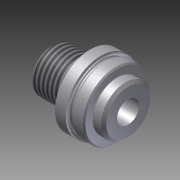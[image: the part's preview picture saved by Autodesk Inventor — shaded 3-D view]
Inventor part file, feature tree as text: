
AUTODESK INVENTOR PART (.ipt)
format: ipt  version: 2012 (Build 160160000, 160)  size: 204,288 bytes
history: native  units: in
note: dims shown in document units (in); Inventor stores cm internally (conversion verified against a paired STEP export)
features: other x70, sketch x5, revolve x4, thread x1, hole x1
ambient origin geometry x8: Origin, YZ Plane, XZ Plane, XY Plane, X Axis, Y Axis, Z Axis, Center Point
bodies: Solid1 (feature_tree)
feature tree (81):
  revolve  "Revolution1"  [1 undecoded]
  thread  "Thread1"  [1 undecoded]
  revolve  "Revolution2"  Angle=360.0deg
  revolve  "Revolution3"  [1 undecoded]
  hole  "Drilling 1"  [1 undecoded]
  revolve  "Revolution4"  [1 undecoded]
  other  "rod_guide_XY"
  other  "rod_guide_YZ"
  other  "rod_guide_ZX"
  other  "rod_guide_X"
  other  "rod_guide_Y"
  other  "rod_guide_Z"
  other  "rod_guide_Center"
  other  "to_tube_XY"
  other  "to_tube_YZ"
  other  "to_tube_ZX"
  other  "to_tube_X"
  other  "to_tube_Y"
  other  "to_tube_Z"
  other  "to_tube_Center"
  other  "to_foot_bracket_XY"
  other  "to_foot_bracket_YZ"
  other  "to_foot_bracket_ZX"
  other  "to_foot_bracket_X"
  other  "to_foot_bracket_Y"
  other  "to_foot_bracket_Z"
  other  "to_foot_bracket_Center"
  other  "to_nut_XY"
  other  "to_nut_YZ"
  other  "to_nut_ZX"
  other  "to_nut_X"
  other  "to_nut_Y"
  other  "to_nut_Z"
  other  "to_nut_Center"
  other  "to_trunnion_brackets_XY"
  other  "to_trunnion_brackets_YZ"
  other  "to_trunnion_brackets_ZX"
  other  "to_trunnion_brackets_X"
  other  "to_trunnion_brackets_Y"
  other  "to_trunnion_brackets_Z"
  other  "to_trunnion_brackets_Center"
  other  "to_trunnion_brackets1_XY"
  other  "to_trunnion_brackets1_YZ"
  other  "to_trunnion_brackets1_ZX"
  other  "to_trunnion_brackets1_X"
  other  "to_trunnion_brackets1_Y"
  other  "to_trunnion_brackets1_Z"
  other  "to_trunnion_brackets1_Center"
  other  "to_trunnion_brackets2_XY"
  other  "to_trunnion_brackets2_YZ"
  other  "to_trunnion_brackets2_ZX"
  other  "to_trunnion_brackets2_X"
  other  "to_trunnion_brackets2_Y"
  other  "to_trunnion_brackets2_Z"
  other  "to_trunnion_brackets2_Center"
  other  "t111_XY"
  other  "t111_YZ"
  other  "t111_ZX"
  other  "t111_X"
  other  "t111_Y"
  other  "t111_Z"
  other  "t111_Center"
  other  "t1_XY"
  other  "t1_YZ"
  other  "t1_ZX"
  other  "t1_X"
  other  "t1_Y"
  other  "t1_Z"
  other  "t1_Center"
  other  "to_screw_XY"
  other  "to_screw_YZ"
  other  "to_screw_ZX"
  other  "to_screw_X"
  other  "to_screw_Y"
  other  "to_screw_Z"
  other  "to_screw_Center"
  sketch  "Sketch_1"  dims[d0=360.0deg d1=0.4083in d2=0.0in d3=360.0deg]
  sketch  "Sketch_3"  dims[d4=360.0deg]
  sketch  "Sketch_4"  dims[d5=0.2535in d6=0.75in d7=0.2735in d8=0.25in d9=90.0deg d10=0.875in d11=0.0in d12=360.0deg]
  sketch  "Sketch4"
  sketch  "Sketch_47"
note: 5 required parameter values undecoded (feature->parameter linkage not recoverable at this tier; creation-order binding heuristic only, values carry confidence <= 0.55)